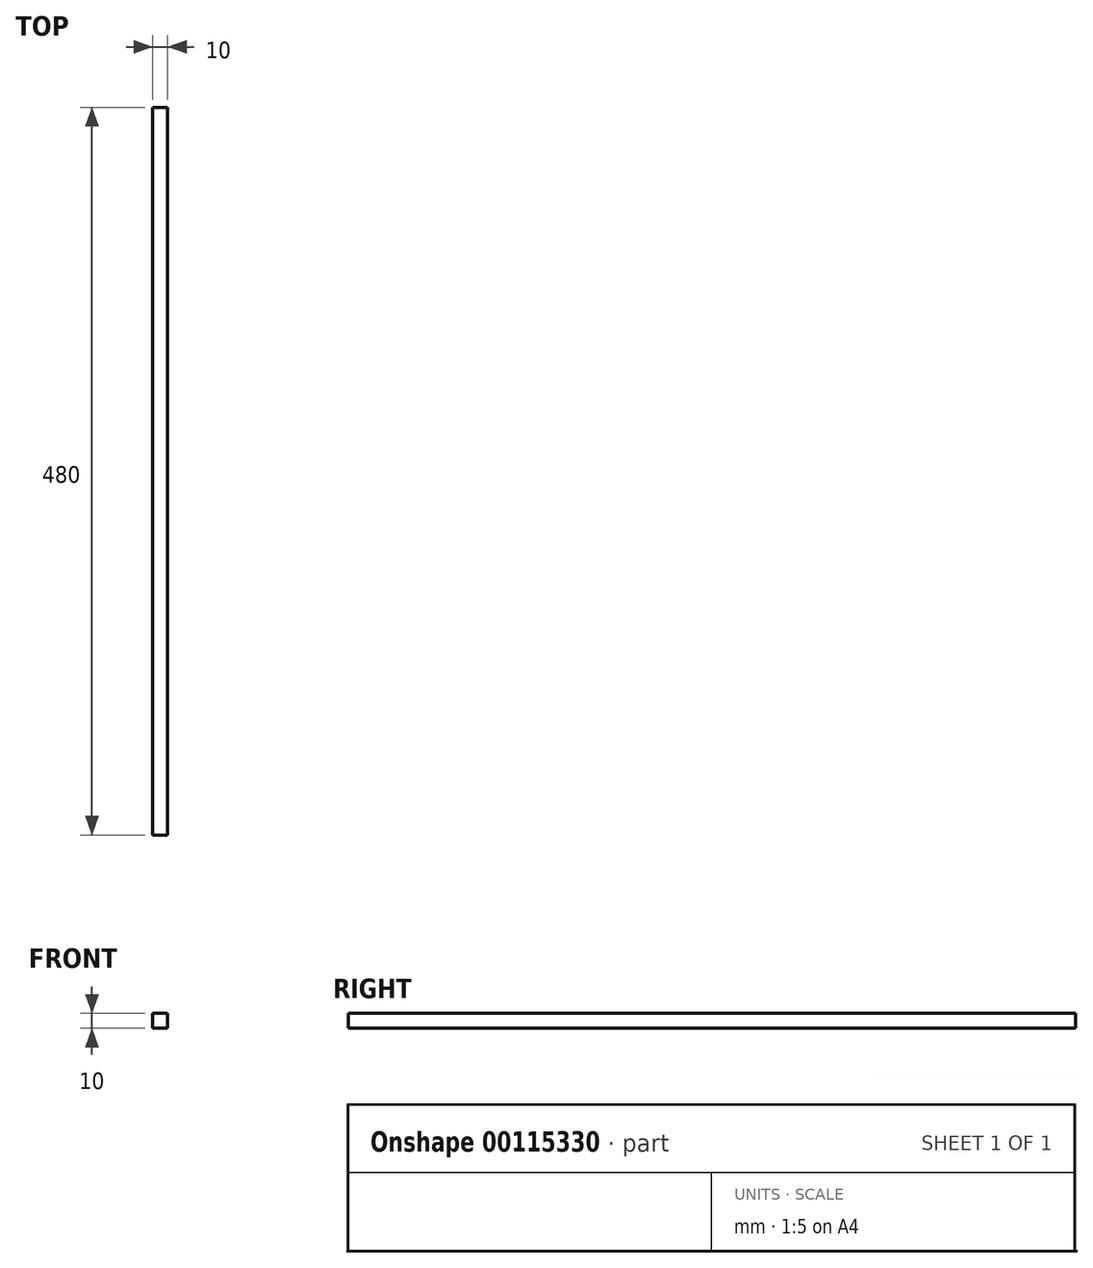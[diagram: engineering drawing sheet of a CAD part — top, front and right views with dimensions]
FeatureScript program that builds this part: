
annotation { "Feature Type Name" : "Feature", "Feature Type Description" : "" }
export const myFeature = defineFeature(function(context is Context, id is Id, definition is map)
    precondition{}
    {
        {
            var Q0;
            Q0=qCreatedBy(makeId("Top.planeOp"),FACE);
            var sketch = newSketch(context, id + "F0", { "sketchPlane" : qUnion([Q0])});
            skLineSegment(sketch, "E0.bottom", {"start": v(0, 0) * mm, "end": v(10, 0) * mm});
            skLineSegment(sketch, "E0.top", {"start": v(0, 480) * mm, "end": v(10, 480) * mm});
            skLineSegment(sketch, "E0.left", {"start": v(0, 0) * mm, "end": v(0, 480) * mm});
            skLineSegment(sketch, "E0.right", {"start": v(10, 0) * mm, "end": v(10, 480) * mm});
            skSolve(sketch);
        }
        {
            var Q0;
            Q0=makeQuery(id+"F0.imprint","IMPRINT",FACE,{"disambiguationData":[TD([[makeQuery(id+"F0.imprint","IMPRINT",EDGE,{"derivedFrom":sQuery(id+"F0.wireOp",EDGE,"E0.bottom")}),1.0]])]});
            extrude(context, id + "F1", {"entities" : qUnion([Q0]), "depth" : 10 * mm});
        }
    });
